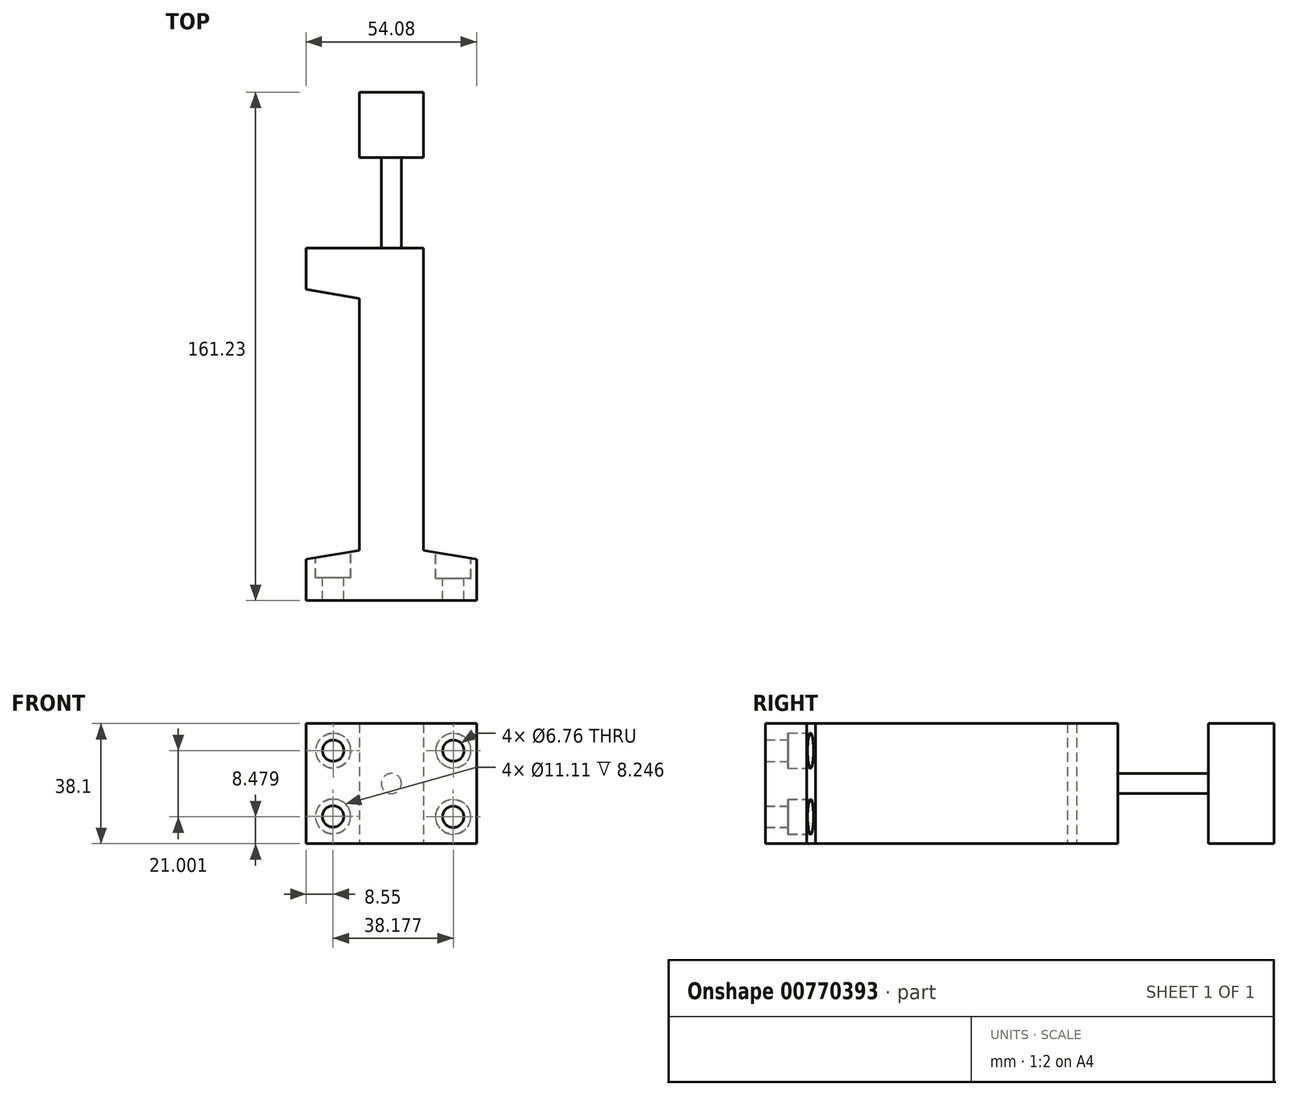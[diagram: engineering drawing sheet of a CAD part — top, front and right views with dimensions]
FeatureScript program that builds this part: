
annotation { "Feature Type Name" : "Feature", "Feature Type Description" : "" }
export const myFeature = defineFeature(function(context is Context, id is Id, definition is map)
    precondition{}
    {
        {
            var Q0;
            Q0=qCreatedBy(makeId("Top.planeOp"),FACE);
            var sketch = newSketch(context, id + "F0", { "sketchPlane" : qUnion([Q0])});
            skText(sketch, "E0", { "text": "i", "fontName": "RobotoSlab-Regular.ttf"});
            const initialGuessF0  = {"E0": [-0.03812, 0, 1, 0, 0.1524]};
            skSetInitialGuess(sketch, initialGuessF0);
            skSolve(sketch);
        }
        {
            var Q0;
            Q0 = qSketchRegion(id + "F0", true);
            extrude(context, id + "F1", {"entities" : qUnion([Q0]), "depth" : 38.1 * mm, "offsetDistance" : 25 * mm});
        }
        {
            var Q0;
            Q0=makeQuery(id+"F1.opExtrude","SWEPT_FACE",FACE,{"disambiguationData":[OSD([sQuery(id+"F0.wireOp",EDGE,"E0.sketch_text.stroke-10")])]});
            var sketch = newSketch(context, id + "F2", { "sketchPlane" : qUnion([Q0])});
            skPoint(sketch, "E1.centerSnap0", {"position": v(8.28, 19.05) * mm});
            skCircle(sketch, "E2", {"center": v(-1.89, 19.05) * mm, "radius": 3.17 * mm});
            skSolve(sketch);
        }
        {
            var Q0;
            Q0=makeQuery(id+"F2.imprint","IMPRINT",FACE,{"disambiguationData":[TD([[makeQuery(id+"F2.imprint","IMPRINT",EDGE,{"derivedFrom":sQuery(id+"F2.wireOp",EDGE,"E2")}),1.0]])]});
            var Q1;
            Q1=sQuery(id+"F2.wireOp",EDGE,"E1");
            extrude(context, id + "F3", {"entities" : qUnion([Q0]), "operationType" : NewBodyOperationType.ADD, "surfaceEntities" : qUnion([Q1]), "depth" : 28.64 * mm, "offsetDistance" : 25 * mm});
        }
        {
            var Q0;
            Q0=makeQuery(id+"F1.opExtrude","SWEPT_FACE",FACE,{"disambiguationData":[OSD([sQuery(id+"F0.wireOp",EDGE,"E0.sketch_text.stroke-8")])]});
            var sketch = newSketch(context, id + "F4", { "sketchPlane" : qUnion([Q0])});
            skCircle(sketch, "E3", {"center": v(-20.3, 29.48) * mm, "radius": 3.38 * mm});
            skCircle(sketch, "E4", {"center": v(17.8, 29.48) * mm, "radius": 3.38 * mm});
            skCircle(sketch, "E5", {"center": v(-20.3, 8.62) * mm, "radius": 3.38 * mm});
            skCircle(sketch, "E6", {"center": v(17.8, 8.48) * mm, "radius": 3.38 * mm});
            skSolve(sketch);
        }
        {
            var Q0;
            Q0=makeQuery(id+"F4.imprint","IMPRINT",FACE,{"disambiguationData":[TD([[makeQuery(id+"F4.imprint","IMPRINT",EDGE,{"derivedFrom":sQuery(id+"F4.wireOp",EDGE,"E3")}),-1.0]])]});
            var Q1;
            Q1 = qBodyType(qCreatedBy(id + "F6" ,EDGE), BodyType.WIRE);
            cPlane(context, id + "F5", {"entities" : qUnion([Q0, Q1]), "cplaneType" : CPlaneType.OFFSET, "offset" : 16 * mm, "oppositeDirection" : true, "width" : 150 * mm, "height" : 150 * mm});
        }
        {
            var Q0;
            Q0=qCreatedBy(id+"F5.planeOp",FACE);
            var sketch = newSketch(context, id + "F6", { "sketchPlane" : qUnion([Q0])});
            skCircle(sketch, "E7", {"center": v(-20.3, 29.48) * mm, "radius": 3.38 * mm});
            skCircle(sketch, "E8", {"center": v(17.8, 29.48) * mm, "radius": 3.38 * mm});
            skCircle(sketch, "E9", {"center": v(-20.38, 8.62) * mm, "radius": 3.38 * mm});
            skCircle(sketch, "E10", {"center": v(17.72, 8.48) * mm, "radius": 3.38 * mm});
            skSolve(sketch);
        }
        {
            var Q0;
            Q0=sQuery(id+"F6.wireOp",VERTEX,"E9.center");
            var Q1;
            Q1=sQuery(id+"F6.wireOp",VERTEX,"E10.center");
            var Q2;
            Q2=sQuery(id+"F6.wireOp",VERTEX,"E8.center");
            var Q3;
            Q3=sQuery(id+"F6.wireOp",VERTEX,"E7.center");
            var Q4;
            Q4=makeQuery(id+"F1.opExtrude","SWEPT_BODY",BODY,{"disambiguationData":[OSD([sQuery(id+"F0.wireOp",EDGE,"E0.sketch_text.stroke-0"),sQuery(id+"F0.wireOp",EDGE,"E0.sketch_text.stroke-1"),sQuery(id+"F0.wireOp",EDGE,"E0.sketch_text.stroke-2"),sQuery(id+"F0.wireOp",EDGE,"E0.sketch_text.stroke-3"),sQuery(id+"F0.wireOp",EDGE,"E0.sketch_text.stroke-4"),sQuery(id+"F0.wireOp",EDGE,"E0.sketch_text.stroke-5"),sQuery(id+"F0.wireOp",EDGE,"E0.sketch_text.stroke-6"),sQuery(id+"F0.wireOp",EDGE,"E0.sketch_text.stroke-7"),sQuery(id+"F0.wireOp",EDGE,"E0.sketch_text.stroke-8"),sQuery(id+"F0.wireOp",EDGE,"E0.sketch_text.stroke-9")])]});
            hole(context, id + "F7", {"style" : HoleStyle.C_BORE, "endStyle" : HoleEndStyle.THROUGH, "oppositeDirection" : true, "holeDiameter" : 6.76 * mm, "cBoreDiameter" : 11.1 * mm, "cBoreDepth" : 6.35 * mm, "majorDiameter" : 5 * mm, "isTappedThrough" : true, "tappedDepth" : 12 * mm, "tapClearance" : 3, "locations" : qUnion([Q0, Q1, Q2, Q3]), "scope" : qUnion([Q4])});
        }
    });
